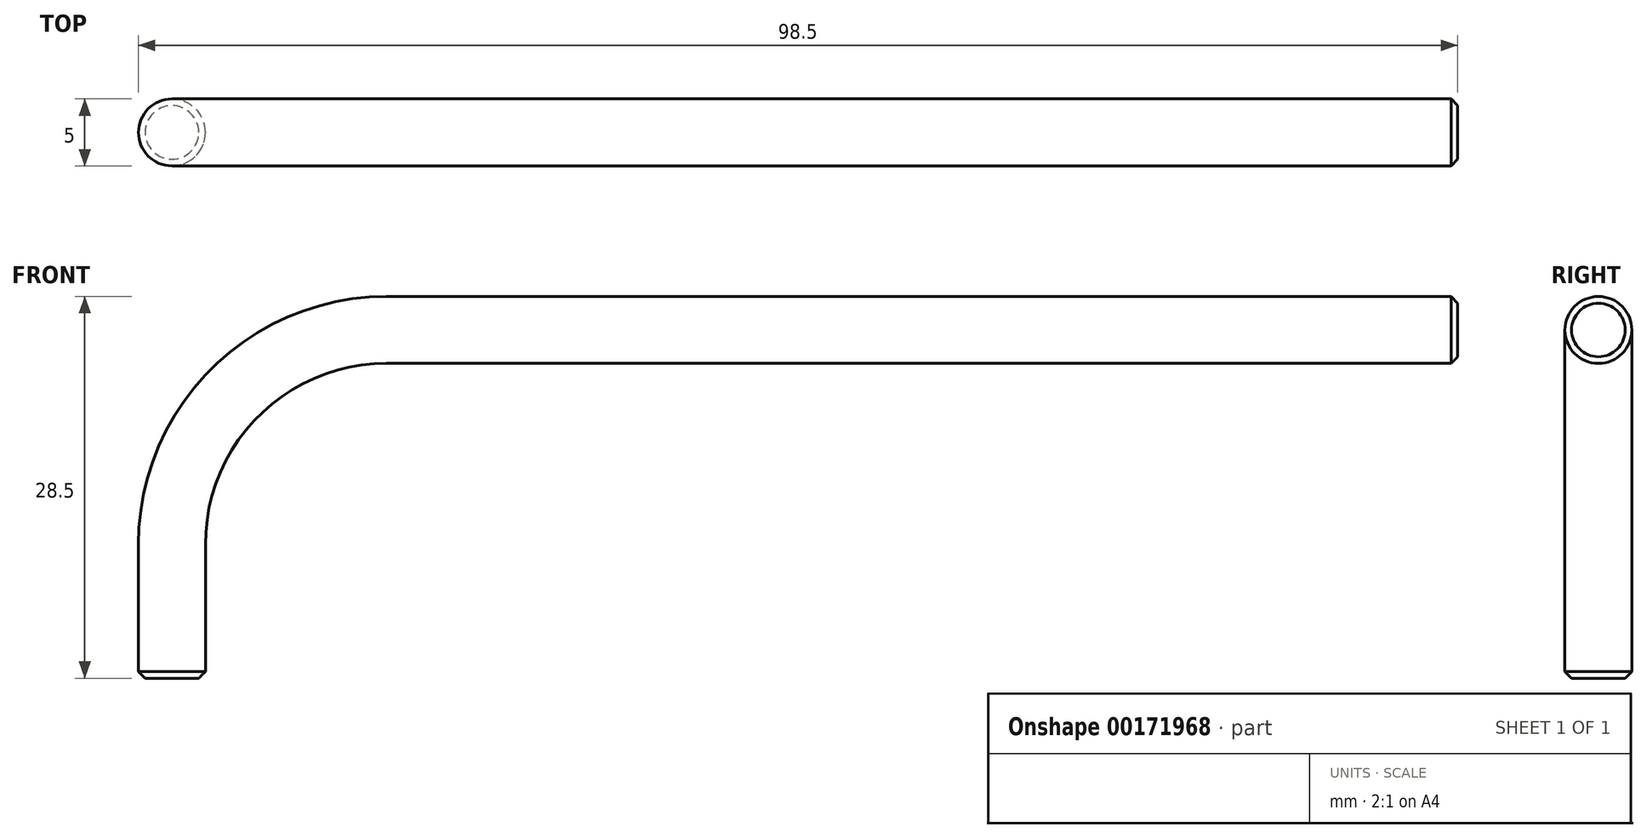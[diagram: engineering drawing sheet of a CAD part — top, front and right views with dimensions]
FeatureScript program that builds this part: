
annotation { "Feature Type Name" : "Feature", "Feature Type Description" : "" }
export const myFeature = defineFeature(function(context is Context, id is Id, definition is map)
    precondition{}
    {
        {
            var Q0;
            Q0=qCreatedBy(makeId("Front.planeOp"),FACE);
            var sketch = newSketch(context, id + "F0", { "sketchPlane" : qUnion([Q0])});
            skLineSegment(sketch, "E0", {"start": v(0, 0) * mm, "end": v(0, 10) * mm});
            skLineSegment(sketch, "E1", {"start": v(16, 26) * mm, "end": v(96, 26) * mm});
            skPoint(sketch, "E2.visualSharp", {"position": v(0, 26) * mm});
            skArc(sketch, "E2.filletArc", {"start": v(16, 26) * mm, "mid": v(4.69, 21.31) * mm, "end": v(0, 10) * mm});
            skSolve(sketch);
        }
        {
            var Q0;
            Q0=qCreatedBy(makeId("Top.planeOp"),FACE);
            var sketch = newSketch(context, id + "F1", { "sketchPlane" : qUnion([Q0])});
            skCircle(sketch, "E3", {"center": v(0, 0) * mm, "radius": 2.5 * mm});
            skSolve(sketch);
        }
        {
            var Q0;
            Q0 = qSketchRegion(id + "F1", true);
            var Q1;
            Q1 = qConstructionFilter(qBodyType(qCreatedBy(id + "F0" ,EDGE), BodyType.WIRE), ConstructionObject.NO);
            sweep(context, id + "F2", {"profiles" : qUnion([Q0]), "path" : qUnion([Q1])});
        }
        {
            var Q0;
            Q0=makeQuery(id+"F2.opSweep","CAP_EDGE",EDGE,{"disambiguationData":[OSD([sQuery(id+"F0.wireOp",VERTEX,"E0.start"),sQuery(id+"F1.wireOp",EDGE,"E3")])],"isStart":true});
            var Q1;
            Q1=makeQuery(id+"F2.opSweep","CAP_EDGE",EDGE,{"disambiguationData":[OSD([sQuery(id+"F0.wireOp",VERTEX,"E1.end"),sQuery(id+"F1.wireOp",EDGE,"E3")])],"isStart":false});
            chamfer(context, id + "F3", {"entities" : qUnion([Q0, Q1]), "chamferType" : ChamferType.OFFSET_ANGLE, "width" : .5 * mm, "oppositeDirection" : false, "angle" : 45 * degree, "tangentPropagation" : true});
        }
    });
